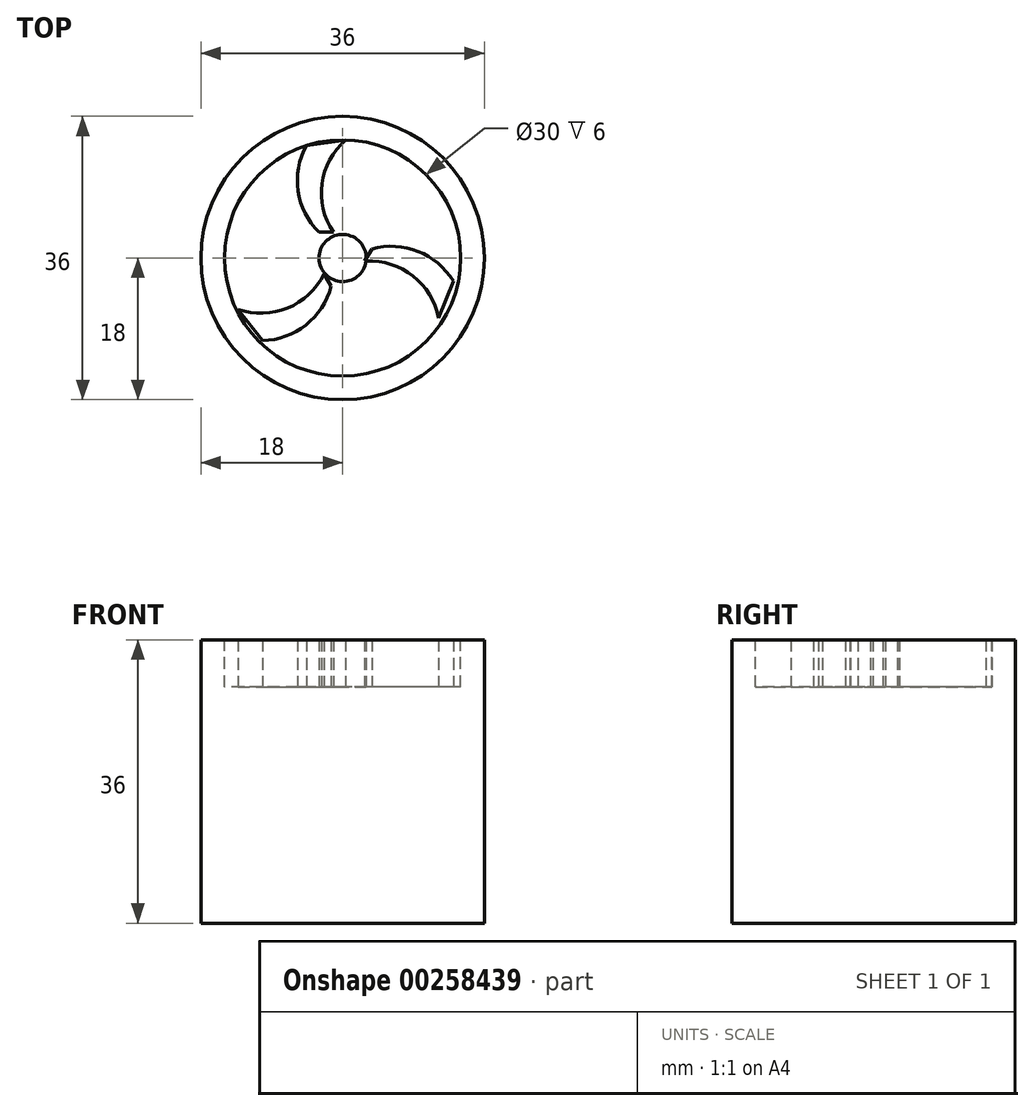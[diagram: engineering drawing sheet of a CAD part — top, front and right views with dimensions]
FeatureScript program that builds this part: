
annotation { "Feature Type Name" : "Feature", "Feature Type Description" : "" }
export const myFeature = defineFeature(function(context is Context, id is Id, definition is map)
    precondition{}
    {
        {
            var Q0;
            Q0=qCreatedBy(makeId("Top.planeOp"),FACE);
            var sketch = newSketch(context, id + "F0", { "sketchPlane" : qUnion([Q0])});
            skCircle(sketch, "E0", {"center": v(0, 0) * mm, "radius": 18 * mm});
            skSolve(sketch);
        }
        {
            var Q0;
            Q0=makeQuery(id+"F0.imprint","IMPRINT",FACE,{"disambiguationData":[TD([[makeQuery(id+"F0.imprint","IMPRINT",EDGE,{"derivedFrom":sQuery(id+"F0.wireOp",EDGE,"E0")}),1.0]])]});
            extrude(context, id + "F1", {"entities" : qUnion([Q0]), "depth" : 36 * mm});
        }
        {
            var Q0;
            Q0=makeQuery(id+"F1.opExtrude","CAP_FACE",FACE,{"disambiguationData":[OSD([sQuery(id+"F0.wireOp",EDGE,"E0")])],"isStart":false});
            var sketch = newSketch(context, id + "F2", { "sketchPlane" : qUnion([Q0])});
            skCircle(sketch, "E1", {"center": v(0, 0) * mm, "radius": 15 * mm});
            skSolve(sketch);
        }
        {
            var Q0;
            Q0=makeQuery(id+"F2.imprint","IMPRINT",FACE,{"disambiguationData":[TD([[makeQuery(id+"F2.imprint","IMPRINT",EDGE,{"derivedFrom":sQuery(id+"F2.wireOp",EDGE,"E1")}),1.0]])]});
            extrude(context, id + "F3", {"entities" : qUnion([Q0]), "operationType" : NewBodyOperationType.REMOVE, "oppositeDirection" : true, "depth" : 6 * mm});
        }
        {
            var Q0;
            Q0=makeQuery(id+"F3.boolean.opBoolean","COPY",FACE,{"derivedFrom":makeQuery(id+"F3.opExtrude","CAP_FACE",FACE,{"disambiguationData":[OSD([sQuery(id+"F2.wireOp",EDGE,"E1")])],"isStart":false})});
            var sketch = newSketch(context, id + "F4", { "sketchPlane" : qUnion([Q0])});
            skLineSegment(sketch, "E2", {"start": v(0, 15) * mm, "end": v(0, 0) * mm, "construction": true});
            skLineSegment(sketch, "E3", {"start": v(-15, 0) * mm, "end": v(14.97, 0) * mm, "construction": true});
            skLineSegment(sketch, "E4.bottom", {"start": v(18, -18) * mm, "end": v(-18, -18) * mm, "construction": true});
            skLineSegment(sketch, "E4.top", {"start": v(18, 18) * mm, "end": v(-18, 18) * mm, "construction": true});
            skLineSegment(sketch, "E4.left", {"start": v(18, -18) * mm, "end": v(18, 18) * mm, "construction": true});
            skLineSegment(sketch, "E4.right", {"start": v(-18, -18) * mm, "end": v(-18, 18) * mm, "construction": true});
            skPoint(sketch, "E4.middle", {"position": v(0, 0) * mm});
            skLineSegment(sketch, "E5", {"start": v(0, 0) * mm, "end": v(0, -15) * mm, "construction": true});
            skLineSegment(sketch, "E6", {"start": v(-18, 18) * mm, "end": v(-18, 18) * mm});
            skPoint(sketch, "E7.2.internal.snap0", {"position": v(0, 7.5) * mm});
            skCircle(sketch, "E8.0", {"center": v(0, 0) * mm, "radius": 20 * mm});
            skArc(sketch, "E9", {"start": v(-4.6, 14.28) * mm, "mid": v(-5.64, 8.5) * mm, "end": v(-2.98, 3.27) * mm});
            skArc(sketch, "E10", {"start": v(0.4, 15) * mm, "mid": v(-2.62, 9.43) * mm, "end": v(-1.18, 3.27) * mm});
            skLineSegment(sketch, "E11", {"start": v(-4.6, 14.28) * mm, "end": v(0.4, 15) * mm});
            skLineSegment(sketch, "E12", {"start": v(-2.98, 3.27) * mm, "end": v(-1.18, 3.27) * mm});
            skLineSegment(sketch, "E13.1.0", {"start": v(-10.19, -10.49) * mm, "end": v(-13.3, -6.52) * mm});
            skArc(sketch, "E13.1.1", {"start": v(-10.19, -10.49) * mm, "mid": v(-4.66, -8.5) * mm, "end": v(-1.46, -3.59) * mm});
            skArc(sketch, "E13.1.2", {"start": v(-13.3, -6.52) * mm, "mid": v(-6.98, -6.35) * mm, "end": v(-2.36, -2.02) * mm});
            skLineSegment(sketch, "E13.1.3", {"start": v(-1.46, -3.59) * mm, "end": v(-2.36, -2.02) * mm});
            skLineSegment(sketch, "E13.2.0", {"start": v(14.06, -2.95) * mm, "end": v(12.18, -7.63) * mm});
            skArc(sketch, "E13.2.1", {"start": v(14.06, -2.95) * mm, "mid": v(9.58, 0.84) * mm, "end": v(3.72, 1.16) * mm});
            skArc(sketch, "E13.2.2", {"start": v(12.18, -7.63) * mm, "mid": v(8.87, -2.24) * mm, "end": v(2.82, -0.4) * mm});
            skLineSegment(sketch, "E13.2.3", {"start": v(3.72, 1.16) * mm, "end": v(2.82, -0.4) * mm});
            skPoint(sketch, "E13.center", {"position": v(-0.24, 0.28) * mm});
            skCircle(sketch, "E14", {"center": v(0, 0) * mm, "radius": 3 * mm});
            skSolve(sketch);
        }
        {
            var Q0;
            Q0=makeQuery(id+"F4.imprint","IMPRINT",FACE,{"disambiguationData":[TD([[makeQuery(id+"F4.imprint","IMPRINT",EDGE,{"derivedFrom":sQuery(id+"F4.wireOp",EDGE,"E13.1.0")}),-1.0]])]});
            var Q1;
            {var subQ5=sQuery(id+"F4.wireOp",EDGE,"E13.2.0");Q1=makeQuery(id+"F4.imprint","IMPRINT",FACE,{"disambiguationData":[TD([[makeQuery(id+"F4.imprint","IMPRINT",EDGE,{"derivedFrom":subQ5}),-1.0]])]});}
            var Q2;
            {var subQ0=sQuery(id+"F4.wireOp",EDGE,"E13.2.3");var subQ1=sQuery(id+"F4.wireOp",EDGE,"E13.2.2");var subQ2=makeQuery(id+"F4.imprint","INTERSECT",VERTEX,{"derivedFrom":[subQ1,subQ0]});Q2=makeQuery(id+"F4.imprint","IMPRINT",FACE,{"disambiguationData":[TD([[makeQuery(id+"F4.imprint","IMPRINT",EDGE,{"disambiguationData":[TD([[subQ2,1.0]])],"derivedFrom":subQ1}),1.0]])]});}
            var Q3;
            Q3=makeQuery(id+"F4.imprint","IMPRINT",FACE,{"disambiguationData":[TD([[makeQuery(id+"F4.imprint","IMPRINT",EDGE,{"derivedFrom":sQuery(id+"F4.wireOp",EDGE,"E9")}),1.0]])]});
            extrude(context, id + "F5", {"entities" : qUnion([Q0, Q1, Q2, Q3]), "depth" : 6 * mm});
        }
    });
